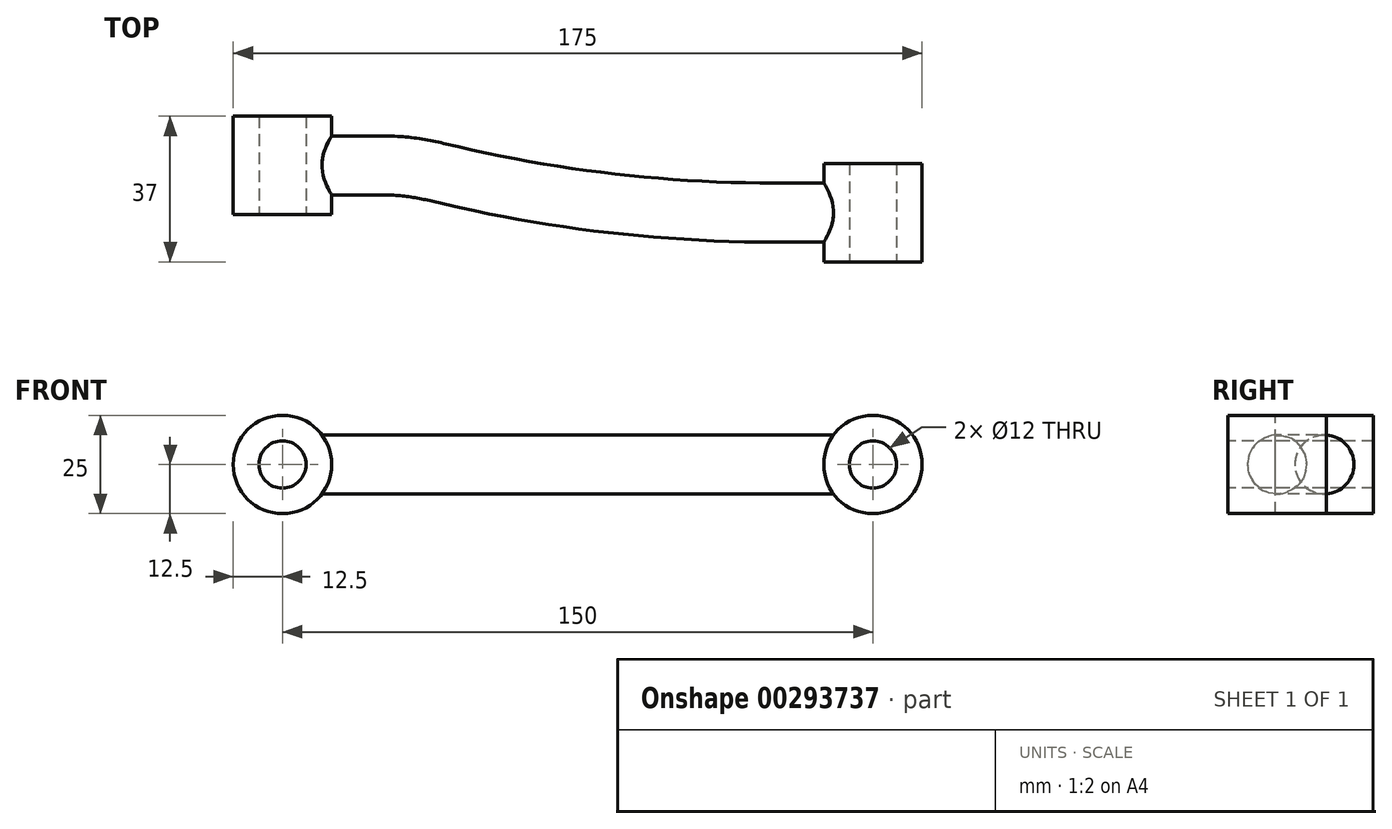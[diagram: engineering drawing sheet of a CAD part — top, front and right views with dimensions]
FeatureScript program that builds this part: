
annotation { "Feature Type Name" : "Feature", "Feature Type Description" : "" }
export const myFeature = defineFeature(function(context is Context, id is Id, definition is map)
    precondition{}
    {
        {
            var Q0;
            Q0=qCreatedBy(makeId("Top.planeOp"),FACE);
            var sketch = newSketch(context, id + "F0", { "sketchPlane" : qUnion([Q0])});
            skLineSegment(sketch, "E0", {"start": v(0, 0) * mm, "end": v(150, 0) * mm, "construction": true});
            skLineSegment(sketch, "E1", {"start": v(150, 0) * mm, "end": v(150, -12) * mm, "construction": true});
            skLineSegment(sketch, "E2", {"start": v(150, -12) * mm, "end": v(125, -12) * mm});
            skLineSegment(sketch, "E3", {"start": v(0, 0) * mm, "end": v(25, 0) * mm});
            skArc(sketch, "E4", {"start": v(25, 0) * mm, "mid": v(32.15, -0.43) * mm, "end": v(39.2, -1.7) * mm});
            skArc(sketch, "E5", {"start": v(39.2, -1.7) * mm, "mid": v(81.79, -9.42) * mm, "end": v(125, -12) * mm});
            skSolve(sketch);
        }
        {
            var Q0;
            Q0=qCreatedBy(makeId("Right.planeOp"),FACE);
            var sketch = newSketch(context, id + "F1", { "sketchPlane" : qUnion([Q0])});
            skCircle(sketch, "E6", {"center": v(0, 0) * mm, "radius": 7.5 * mm});
            skSolve(sketch);
        }
        {
            var Q0;
            Q0=makeQuery(id+"F1.imprint","IMPRINT",FACE,{"disambiguationData":[TD([[makeQuery(id+"F1.imprint","IMPRINT",EDGE,{"derivedFrom":sQuery(id+"F1.wireOp",EDGE,"E6")}),1.0]])]});
            var Q1;
            Q1 = qConstructionFilter(qBodyType(qCreatedBy(id + "F0" ,EDGE), BodyType.WIRE), ConstructionObject.NO);
            sweep(context, id + "F2", {"profiles" : qUnion([Q0]), "path" : qUnion([Q1])});
        }
        {
            var Q0;
            Q0=qCreatedBy(makeId("Front.planeOp"),FACE);
            var sketch = newSketch(context, id + "F3", { "sketchPlane" : qUnion([Q0])});
            skCircle(sketch, "E7", {"center": v(0, 0) * mm, "radius": 12.5 * mm});
            skSolve(sketch);
        }
        {
            var Q0;
            Q0 = qSketchRegion(id + "F3", true);
            extrude(context, id + "F4", {"entities" : qUnion([Q0]), "operationType" : NewBodyOperationType.ADD, "endBound" : BoundingType.SYMMETRIC, "depth" : 25 * mm});
        }
        {
            var Q0;
            Q0=makeQuery(id+"F4.opExtrude","CAP_FACE",FACE,{"disambiguationData":[OSD([sQuery(id+"F3.wireOp",EDGE,"E7")])],"isStart":false});
            var sketch = newSketch(context, id + "F5", { "sketchPlane" : qUnion([Q0])});
            skCircle(sketch, "E8", {"center": v(0, 0) * mm, "radius": 6 * mm});
            skSolve(sketch);
        }
        {
            var Q0;
            Q0 = qSketchRegion(id + "F5", true);
            extrude(context, id + "F6", {"entities" : qUnion([Q0]), "operationType" : NewBodyOperationType.REMOVE, "oppositeDirection" : true, "depth" : 25 * mm});
        }
        {
            var Q0;
            Q0=qCreatedBy(makeId("Front.planeOp"),FACE);
            cPlane(context, id + "F7", {"entities" : qUnion([Q0]), "cplaneType" : CPlaneType.OFFSET, "offset" : 12 * mm, "width" : 150 * mm, "height" : 150 * mm});
        }
        {
            var Q0;
            Q0=qCreatedBy(id+"F7.planeOp",FACE);
            var sketch = newSketch(context, id + "F8", { "sketchPlane" : qUnion([Q0])});
            skLineSegment(sketch, "E9", {"start": v(150, -7.5) * mm, "end": v(125, -7.5) * mm});
            skLineSegment(sketch, "E10", {"start": v(125, 7.5) * mm, "end": v(150, 7.5) * mm});
            skLineSegment(sketch, "E11", {"start": v(150, 7.5) * mm, "end": v(150, -7.5) * mm});
            skCircle(sketch, "E12", {"center": v(150, 0) * mm, "radius": 12.5 * mm});
            skSolve(sketch);
        }
        {
            var Q0;
            Q0 = qSketchRegion(id + "F8", true);
            extrude(context, id + "F9", {"entities" : qUnion([Q0]), "operationType" : NewBodyOperationType.ADD, "endBound" : BoundingType.SYMMETRIC, "depth" : 25 * mm});
        }
        {
            var Q0;
            Q0=makeQuery(id+"F9.opExtrude","CAP_FACE",FACE,{"disambiguationData":[OSD([sQuery(id+"F8.wireOp",EDGE,"E12")])],"isStart":false});
            var sketch = newSketch(context, id + "F10", { "sketchPlane" : qUnion([Q0])});
            skCircle(sketch, "E13", {"center": v(150, 0) * mm, "radius": 6 * mm});
            skSolve(sketch);
        }
        {
            var Q0;
            Q0 = qSketchRegion(id + "F10", true);
            extrude(context, id + "F11", {"entities" : qUnion([Q0]), "operationType" : NewBodyOperationType.REMOVE, "oppositeDirection" : true, "depth" : 25 * mm});
        }
    });
